# Revit family: IS_Tesi_T0077_BIM_ES
name_source: partatom
category: Plumbing Fixtures
units: mm (PartAtom-declared; Revit-internal decimal feet)

## family parameters
Cut with Voids When Loaded = No
Host = Face
OmniClass Number = 23.45.05.21.11.11
OmniClass Title = Water Operated Water Closets
Part Type = Normal
Room Calculation Point = No
Round Connector Dimension = Use Diameter
Shared = No

## types (2) — shared parameters
Accesorios = https://www.idealstandard.es
Assembly Code = C1030200
Autor = Ideal Standard s.l.u. (ESP)
Ayuda = https://www.idealstandard.es
CódigoDeBarras = 8014140435211
DescripciónUniclass2015 = WCPANS
Description = Inodoro a pared TESI tanque alto con Aquablade, blanco
Destacado = Inodoro a pared tanque alto con Aquablade, blanco
Espacio = Interno
FechaDeCreación = 2017-01-28
Forma = Escultural
GarantíaDeLasPiezas = 2
GarantíaPiezas = 2
GuíaDeInstallación = https://www.idealstandard.es
IfcExportaComo = WCPANS
InformaciónDeProducto = https://www.idealstandard.es
Manufacturer = https://www.idealstandard.es
Marca = Ideal Standard Iberia
Material = Porcelana vitrificada
MaterialWc = Porcelana vitrificada
Nombre = WcPans_Tesi_T007701_IdealStandard
NombreDeObjetoBim = IS_IdealStandard_WcPans_Tesi_T0077
NominalHeight = 400 mm  [stored 1.31234 ft]
NominalLength = 550 mm
NominalWidth = 360 mm
NúmeroDeModelo = T007701
PesoNeto = 28.00 Kg
ReferenciaDeModelo = Inodoro a pared tanque alto con Aquablade, blanco
ReferenciaUniclass2015 = Pr_40_20_93_94
Repuestos = https://www.idealstandard.es
Size = 550 x 360 x 400 mm
Teléfono = +34 93 561 80 00
TipoDeConexión = Fontaneria
TipoDeExportaciónIfc = TOILETPAN
TipoDeGarantía = Garantía del Fabricante
TipoDeTaza = Tanque alto
TipoMontajeWc = A suelo / cerrado
TipoWc = 0
URL = https://www.idealstandard.es
UnidadDeVolúmen = Litros
UnidadDeÁrea = milímetros
UnidadGarantía = año
UnidadLineal = milímetros
Versión = 1
zero-valued in all types: CWFU, Cost, Default Elevation, HWFU, NivelDeDesbordamiento, NominalDepth, PesoBruto, WFU

## per-type parameters (varying)
| type | Acabado | Color | ColorWc | Finish | Model | Referencia |
| T007701 - Inodoro a pared TESI tanque alto con Aquablade, blanco | Blanco | Blanco | Blanco | IS_RenderMaterial_VitreousChina_White | T007701 | T007701 |
| T0077V3 - Inodoro a pared TESI tanque alto con Aquablade, Negro Seda | Negro Seda | Negro Seda | Negro Seda | IS_RenderMaterial_VitreousChina_Black_Silk | T0077V3 | T0077V3 |

note: [stored X ft] marks values corroborated as IEEE doubles in the binary element streams (Revit-internal decimal feet)

## geometry (parser evidence)
native form markers: Sweep x3
no freeform markers — native parametric forms only
